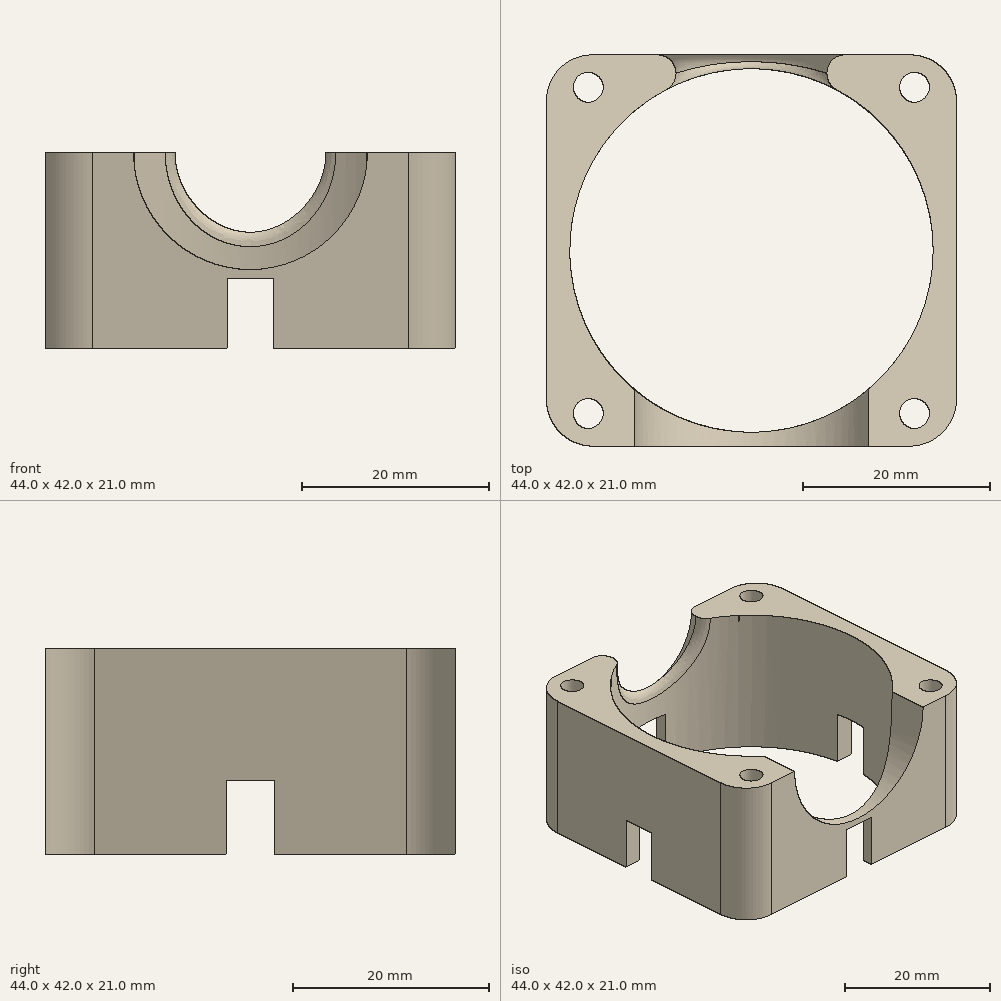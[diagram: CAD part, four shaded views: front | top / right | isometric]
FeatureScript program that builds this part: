
annotation { "Feature Type Name" : "Feature", "Feature Type Description" : "" }
export const myFeature = defineFeature(function(context is Context, id is Id, definition is map)
    precondition{}
    {
        {
            var Q0;
            Q0=qCreatedBy(makeId("Top.planeOp"),FACE);
            var sketch = newSketch(context, id + "F0", { "sketchPlane" : qUnion([Q0])});
            skLineSegment(sketch, "E0.bottom", {"start": v(0, 21) * mm, "end": v(22, 21) * mm});
            skLineSegment(sketch, "E0.top", {"start": v(0, -21) * mm, "end": v(22, -21) * mm});
            skLineSegment(sketch, "E0.left", {"start": v(0, 21) * mm, "end": v(0, -21) * mm});
            skLineSegment(sketch, "E0.right", {"start": v(22, 21) * mm, "end": v(22, -21) * mm});
            skSolve(sketch);
        }
        {
            var Q0;
            Q0=makeQuery(id+"F0.imprint","IMPRINT",FACE,{"disambiguationData":[TD([[makeQuery(id+"F0.imprint","IMPRINT",EDGE,{"derivedFrom":sQuery(id+"F0.wireOp",EDGE,"E0.bottom")}),-1.0]])]});
            extrude(context, id + "F1", {"entities" : qUnion([Q0]), "depth" : 21 * mm});
        }
        {
            var Q0;
            Q0=makeQuery(id+"F1.opExtrude","SWEPT_FACE",FACE,{"disambiguationData":[OSD([sQuery(id+"F0.wireOp",EDGE,"E0.top")])]});
            var sketch = newSketch(context, id + "F2", { "sketchPlane" : qUnion([Q0])});
            skCircle(sketch, "E1", {"center": v(0, 21) * mm, "radius": 12.55 * mm});
            skSolve(sketch);
        }
        {
            var Q0;
            {var subQ0=sQuery(id+"F0.wireOp",EDGE,"E0.bottom");var subQ1=sQuery(id+"F0.wireOp",EDGE,"E0.top");var subQ2=sQuery(id+"F0.wireOp",EDGE,"E0.right");Q0=makeQuery(id+"FA7PMqFMRjNLv7i_1.boolean.opBoolean","SPLIT",FACE,{"disambiguationData":[TD([makeQuery(id+"F1.opExtrude","SWEPT_FACE",FACE,{"disambiguationData":[OSD([subQ2])]})])],"derivedFrom":makeQuery(id+"F1.opExtrude","CAP_FACE",FACE,{"disambiguationData":[OSD([subQ0,subQ1,sQuery(id+"F0.wireOp",EDGE,"E0.left"),subQ2])],"isStart":false})});}
            var sketch = newSketch(context, id + "F3", { "sketchPlane" : qUnion([Q0])});
            skCircle(sketch, "E2", {"center": v(-17.5, -17.5) * mm, "radius": 1.6 * mm});
            skCircle(sketch, "E3", {"center": v(-17.5, 17.5) * mm, "radius": 1.6 * mm});
            skCircle(sketch, "E4", {"center": v(17.5, 17.5) * mm, "radius": 1.6 * mm});
            skCircle(sketch, "E5", {"center": v(17.5, -17.5) * mm, "radius": 1.6 * mm});
            skLineSegment(sketch, "E6", {"start": v(-17.5, 17.5) * mm, "end": v(17.5, 17.5) * mm, "construction": true});
            skLineSegment(sketch, "E7", {"start": v(17.5, -17.5) * mm, "end": v(17.5, 17.5) * mm, "construction": true});
            skLineSegment(sketch, "E8", {"start": v(17.5, -17.5) * mm, "end": v(-17.5, -17.5) * mm, "construction": true});
            skLineSegment(sketch, "E9", {"start": v(-17.5, -17.5) * mm, "end": v(-17.5, 17.5) * mm, "construction": true});
            skLineSegment(sketch, "E10", {"start": v(-17.5, 17.5) * mm, "end": v(17.5, -17.5) * mm, "construction": true});
            skLineSegment(sketch, "E11", {"start": v(17.5, 17.5) * mm, "end": v(-17.5, -17.5) * mm, "construction": true});
            skSolve(sketch);
        }
        {
            var Q0;
            Q0=qSketchRegion(id+"F3",true);
            extrude(context, id + "F4", {"entities" : qUnion([Q0]), "operationType" : NewBodyOperationType.REMOVE, "oppositeDirection" : true, "depth" : 25 * mm});
        }
        {
            var Q0;
            Q0=qSketchRegion(id+"F2",true);
            extrude(context, id + "F5", {"entities" : qUnion([Q0]), "operationType" : NewBodyOperationType.REMOVE, "oppositeDirection" : true, "depth" : 36 * mm});
        }
        {
            var Q0;
            Q0=makeQuery(id+"F5.boolean.opBoolean","COPY",FACE,{"derivedFrom":makeQuery(id+"F5.opExtrude","CAP_FACE",FACE,{"disambiguationData":[OSD([sQuery(id+"F2.wireOp",EDGE,"E1")])],"isStart":false})});
            var sketch = newSketch(context, id + "F6", { "sketchPlane" : qUnion([Q0])});
            skCircle(sketch, "E12", {"center": v(0, 21) * mm, "radius": 8.1 * mm});
            skSolve(sketch);
        }
        {
            var Q0;
            Q0=qSketchRegion(id+"F6",true);
            extrude(context, id + "F7", {"entities" : qUnion([Q0]), "operationType" : NewBodyOperationType.REMOVE, "oppositeDirection" : true, "depth" : 25 * mm});
        }
        {
            var Q0;
            Q0=makeQuery(id+"F1.opExtrude","CAP_FACE",FACE,{"disambiguationData":[OSD([sQuery(id+"F0.wireOp",EDGE,"E0.bottom"),sQuery(id+"F0.wireOp",EDGE,"E0.top"),sQuery(id+"F0.wireOp",EDGE,"E0.left"),sQuery(id+"F0.wireOp",EDGE,"E0.right")])],"isStart":true});
            var sketch = newSketch(context, id + "F8", { "sketchPlane" : qUnion([Q0])});
            skCircle(sketch, "E13", {"center": v(0, 0) * mm, "radius": 19.5 * mm});
            skSolve(sketch);
        }
        {
            var Q0;
            Q0 = qSketchRegion(id + "F8", true);
            extrude(context, id + "F9", {"entities" : qUnion([Q0]), "operationType" : NewBodyOperationType.REMOVE, "oppositeDirection" : true, "depth" : 25 * mm});
        }
        {
            var Q0;
            Q0=qCreatedBy(makeId("Top.planeOp"),FACE);
            var sketch = newSketch(context, id + "F10", { "sketchPlane" : qUnion([Q0])});
            skLineSegment(sketch, "E14.bottom", {"start": v(2.5, -21) * mm, "end": v(-2.5, -21) * mm});
            skLineSegment(sketch, "E14.top", {"start": v(2.5, 21) * mm, "end": v(-2.5, 21) * mm});
            skLineSegment(sketch, "E14.left", {"start": v(2.5, -21) * mm, "end": v(2.5, 21) * mm});
            skLineSegment(sketch, "E14.right", {"start": v(-2.5, -21) * mm, "end": v(-2.5, 21) * mm});
            skLineSegment(sketch, "E15.bottom", {"start": v(2.5, -2.5) * mm, "end": v(22, -2.5) * mm});
            skLineSegment(sketch, "E15.top", {"start": v(2.5, 2.5) * mm, "end": v(22, 2.5) * mm});
            skLineSegment(sketch, "E15.left", {"start": v(2.5, -2.5) * mm, "end": v(2.5, 2.5) * mm});
            skLineSegment(sketch, "E15.right", {"start": v(22, -2.5) * mm, "end": v(22, 2.5) * mm});
            skSolve(sketch);
        }
        {
            var Q0;
            Q0 = qSketchRegion(id + "F10", true);
            extrude(context, id + "F11", {"entities" : qUnion([Q0]), "operationType" : NewBodyOperationType.REMOVE, "depth" : 7.5 * mm});
        }
        {
            var Q0;
            Q0=makeQuery(id+"F1.opExtrude","SWEPT_EDGE",EDGE,{"disambiguationData":[OSD([sQuery(id+"F0.wireOp",EDGE,"E0.top"),sQuery(id+"F0.wireOp",EDGE,"E0.right")])]});
            var Q1;
            Q1=makeQuery(id+"F1.opExtrude","SWEPT_EDGE",EDGE,{"disambiguationData":[OSD([sQuery(id+"F0.wireOp",EDGE,"E0.bottom"),sQuery(id+"F0.wireOp",EDGE,"E0.right")])]});
            fillet(context, id + "F12", {"entities" : qUnion([Q0, Q1]), "radius" : 5 * mm, "tangentPropagation" : true, "allowEdgeOverflow" : false});
        }
        {
            var Q0;
            Q0=makeQuery(id+"F1.opExtrude","SWEPT_BODY",BODY,{"disambiguationData":[OSD([sQuery(id+"F0.wireOp",EDGE,"E0.bottom"),sQuery(id+"F0.wireOp",EDGE,"E0.top"),sQuery(id+"F0.wireOp",EDGE,"E0.left"),sQuery(id+"F0.wireOp",EDGE,"E0.right")])]});
            var Q1;
            Q1=qCreatedBy(makeId("Right.planeOp"),FACE);
            mirror(context, id + "F13", {"operationType" : NewBodyOperationType.ADD, "entities" : qUnion([Q0]), "mirrorPlane" : qUnion([Q1])});
        }
        {
            var Q0;
            {var subQ0=makeQuery(id+"F7.boolean.opBoolean","INTERSECT",EDGE,{"derivedFrom":[makeQuery(id+"F1.opExtrude","SWEPT_FACE",FACE,{"disambiguationData":[OSD([sQuery(id+"F0.wireOp",EDGE,"E0.bottom")])]}),makeQuery(id+"F7.opExtrude","SWEPT_FACE",FACE,{"disambiguationData":[OSD([sQuery(id+"F6.wireOp",EDGE,"E12")])]})]});Q0=makeQuery(id+"F13.boolean.opBoolean","MERGE",EDGE,{"derivedFrom":[subQ0,makeQuery(id+"F13.opPattern","COPY",EDGE,{"derivedFrom":subQ0,"instanceName":"1"})]});}
            var Q1;
            {var subQ0=makeQuery(id+"F9.boolean.opBoolean","INTERSECT",EDGE,{"derivedFrom":[makeQuery(id+"F7.boolean.opBoolean","COPY",FACE,{"derivedFrom":makeQuery(id+"F7.opExtrude","SWEPT_FACE",FACE,{"disambiguationData":[OSD([sQuery(id+"F6.wireOp",EDGE,"E12")])]})}),makeQuery(id+"F9.opExtrude","SWEPT_FACE",FACE,{"disambiguationData":[OSD([sQuery(id+"F8.wireOp",EDGE,"E13")])]})]});Q1=makeQuery(id+"F13.boolean.opBoolean","MERGE",EDGE,{"derivedFrom":[subQ0,makeQuery(id+"F13.opPattern","COPY",EDGE,{"derivedFrom":subQ0,"instanceName":"1"})]});}
            fillet(context, id + "F14", {"entities" : qUnion([Q0, Q1]), "radius" : 2 * mm, "tangentPropagation" : true, "allowEdgeOverflow" : false});
        }
    });
